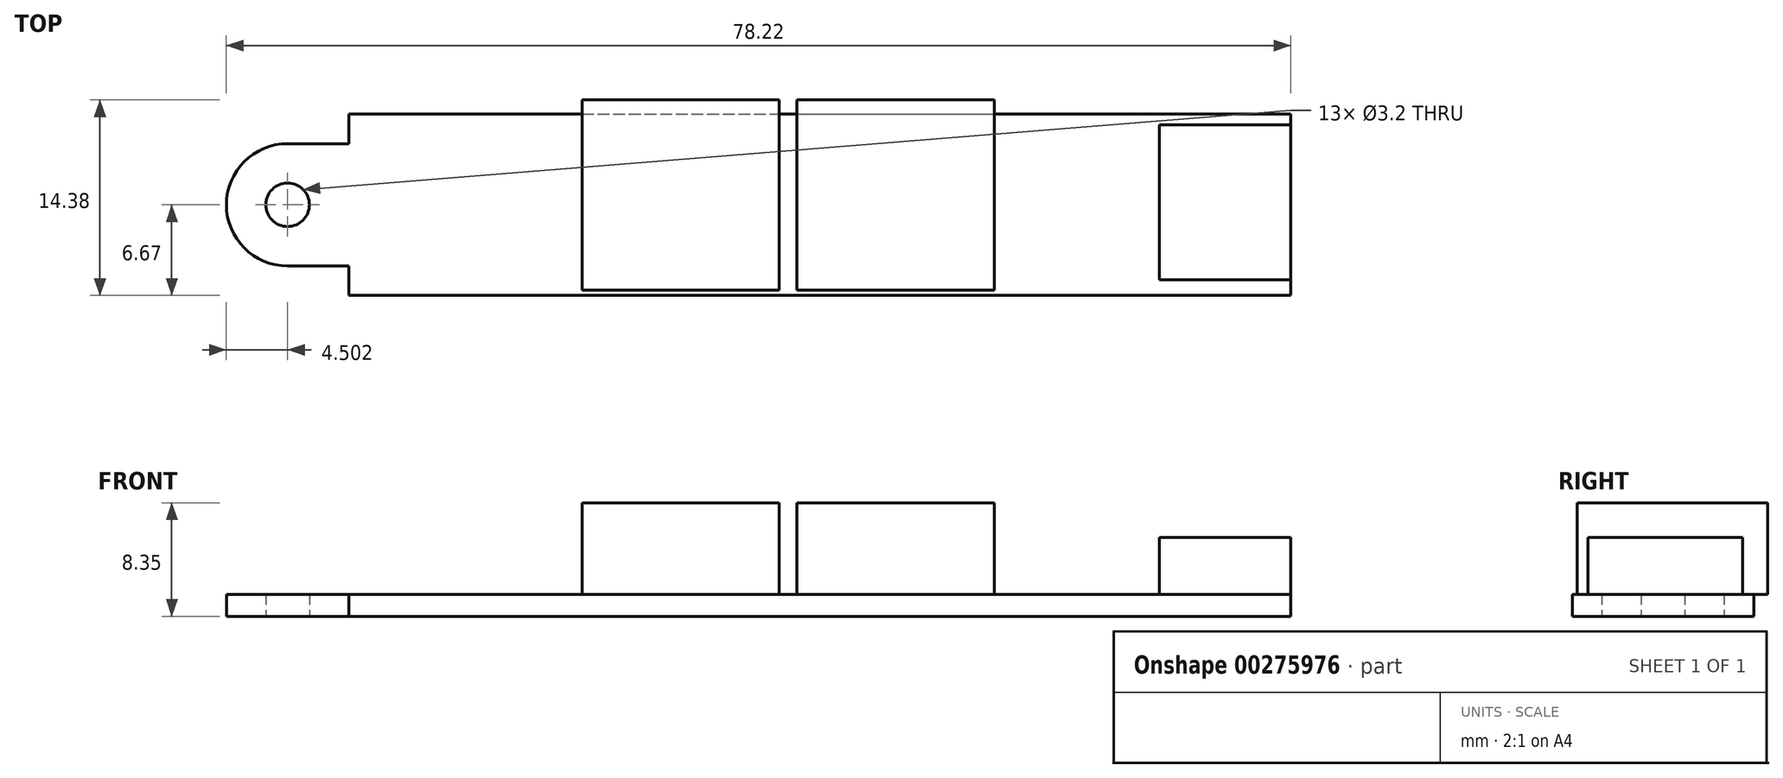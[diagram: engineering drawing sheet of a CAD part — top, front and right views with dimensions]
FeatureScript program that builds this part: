
annotation { "Feature Type Name" : "Feature", "Feature Type Description" : "" }
export const myFeature = defineFeature(function(context is Context, id is Id, definition is map)
    precondition{}
    {
        {
            var Q0;
            Q0=qCreatedBy(makeId("Top.planeOp"),FACE);
            var sketch = newSketch(context, id + "F0", { "sketchPlane" : qUnion([Q0])});
            skLineSegment(sketch, "E0.bottom", {"start": v(-34.6, 6.67) * mm, "end": v(34.6, 6.67) * mm});
            skLineSegment(sketch, "E0.top", {"start": v(-34.6, -6.67) * mm, "end": v(34.6, -6.67) * mm});
            skLineSegment(sketch, "E0.left", {"start": v(-34.6, 6.67) * mm, "end": v(-34.6, -6.67) * mm});
            skLineSegment(sketch, "E0.right", {"start": v(34.6, 6.67) * mm, "end": v(34.6, -6.67) * mm});
            skPoint(sketch, "E1", {"position": v(0, 6.67) * mm});
            skPoint(sketch, "E2", {"position": v(34.6, 0) * mm});
            skCircle(sketch, "E3", {"center": v(-39.1, 0) * mm, "radius": 1.6 * mm});
            skCircle(sketch, "E4", {"center": v(-39.1, 0) * mm, "radius": 4.5 * mm});
            skLineSegment(sketch, "E5", {"start": v(-39.1, 4.5) * mm, "end": v(-34.6, 4.5) * mm});
            skLineSegment(sketch, "E6", {"start": v(-34.6, -4.5) * mm, "end": v(-39.1, -4.5) * mm});
            skSolve(sketch);
        }
        {
            var Q0;
            Q0 = qSketchRegion(id + "F0", true);
            extrude(context, id + "F1", {"entities" : qUnion([Q0]), "depth" : 1.6 * mm});
        }
        {
            var Q0;
            Q0=makeQuery(id+"F1.opExtrude","CAP_FACE",FACE,{"disambiguationData":[OSD([sQuery(id+"F0.wireOp",EDGE,"E0.bottom"),sQuery(id+"F0.wireOp",EDGE,"E0.top"),sQuery(id+"F0.wireOp",EDGE,"E0.left"),sQuery(id+"F0.wireOp",EDGE,"E0.right"),sQuery(id+"F0.wireOp",EDGE,"E3"),sQuery(id+"F0.wireOp",EDGE,"E4"),sQuery(id+"F0.wireOp",EDGE,"E5"),sQuery(id+"F0.wireOp",EDGE,"E6")])],"isStart":false});
            var sketch = newSketch(context, id + "F2", { "sketchPlane" : qUnion([Q0])});
            skLineSegment(sketch, "E7.bottom", {"start": v(-17.48, 7.71) * mm, "end": v(-2.98, 7.71) * mm});
            skLineSegment(sketch, "E7.top", {"start": v(-17.48, -6.29) * mm, "end": v(-2.98, -6.29) * mm});
            skLineSegment(sketch, "E7.left", {"start": v(-17.48, 7.71) * mm, "end": v(-17.48, -6.29) * mm});
            skLineSegment(sketch, "E7.right", {"start": v(-2.98, 7.71) * mm, "end": v(-2.98, -6.29) * mm});
            skLineSegment(sketch, "E8.bottom", {"start": v(-1.68, 7.71) * mm, "end": v(12.82, 7.71) * mm});
            skLineSegment(sketch, "E8.top", {"start": v(-1.68, -6.29) * mm, "end": v(12.82, -6.29) * mm});
            skLineSegment(sketch, "E8.left", {"start": v(-1.68, 7.71) * mm, "end": v(-1.68, -6.29) * mm});
            skLineSegment(sketch, "E8.right", {"start": v(12.82, 7.71) * mm, "end": v(12.82, -6.29) * mm});
            skSolve(sketch);
        }
        {
            var Q0;
            {var subQ0=sQuery(id+"F2.wireOp",EDGE,"E7.top");Q0=makeQuery(id+"F2.imprint","IMPRINT",FACE,{"disambiguationData":[TD([[makeQuery(id+"F2.imprint","IMPRINT",EDGE,{"derivedFrom":subQ0}),1.0]])]});}
            var Q1;
            {var subQ0=sQuery(id+"F2.wireOp",EDGE,"E7.bottom");Q1=makeQuery(id+"F2.imprint","IMPRINT",FACE,{"disambiguationData":[TD([[makeQuery(id+"F2.imprint","IMPRINT",EDGE,{"derivedFrom":subQ0}),-1.0]])]});}
            var Q2;
            {var subQ0=sQuery(id+"F2.wireOp",EDGE,"E8.bottom");Q2=makeQuery(id+"F2.imprint","IMPRINT",FACE,{"disambiguationData":[TD([[makeQuery(id+"F2.imprint","IMPRINT",EDGE,{"derivedFrom":subQ0}),-1.0]])]});}
            var Q3;
            {var subQ0=sQuery(id+"F2.wireOp",EDGE,"E8.top");Q3=makeQuery(id+"F2.imprint","IMPRINT",FACE,{"disambiguationData":[TD([[makeQuery(id+"F2.imprint","IMPRINT",EDGE,{"derivedFrom":subQ0}),1.0]])]});}
            extrude(context, id + "F3", {"entities" : qUnion([Q0, Q1, Q2, Q3]), "depth" : 6.75 * mm});
        }
        {
            var Q0;
            Q0=makeQuery(id+"F1.opExtrude","CAP_FACE",FACE,{"disambiguationData":[OSD([sQuery(id+"F0.wireOp",EDGE,"E0.bottom"),sQuery(id+"F0.wireOp",EDGE,"E0.top"),sQuery(id+"F0.wireOp",EDGE,"E0.left"),sQuery(id+"F0.wireOp",EDGE,"E0.right"),sQuery(id+"F0.wireOp",EDGE,"E3"),sQuery(id+"F0.wireOp",EDGE,"E4"),sQuery(id+"F0.wireOp",EDGE,"E5"),sQuery(id+"F0.wireOp",EDGE,"E6")])],"isStart":false});
            var sketch = newSketch(context, id + "F4", { "sketchPlane" : qUnion([Q0])});
            skLineSegment(sketch, "E9.bottom", {"start": v(34.6, 5.87) * mm, "end": v(24.94, 5.87) * mm});
            skLineSegment(sketch, "E9.top", {"start": v(34.6, -5.51) * mm, "end": v(24.94, -5.51) * mm});
            skLineSegment(sketch, "E9.left", {"start": v(34.6, 5.87) * mm, "end": v(34.6, -5.51) * mm});
            skLineSegment(sketch, "E9.right", {"start": v(24.94, 5.87) * mm, "end": v(24.94, -5.51) * mm});
            skSolve(sketch);
        }
        {
            var Q0;
            Q0=makeQuery(id+"F4.imprint","IMPRINT",FACE,{"disambiguationData":[TD([[makeQuery(id+"F4.imprint","IMPRINT",EDGE,{"derivedFrom":sQuery(id+"F4.wireOp",EDGE,"E9.bottom")}),1.0]])]});
            extrude(context, id + "F5", {"entities" : qUnion([Q0]), "depth" : 4.2 * mm});
        }
    });
